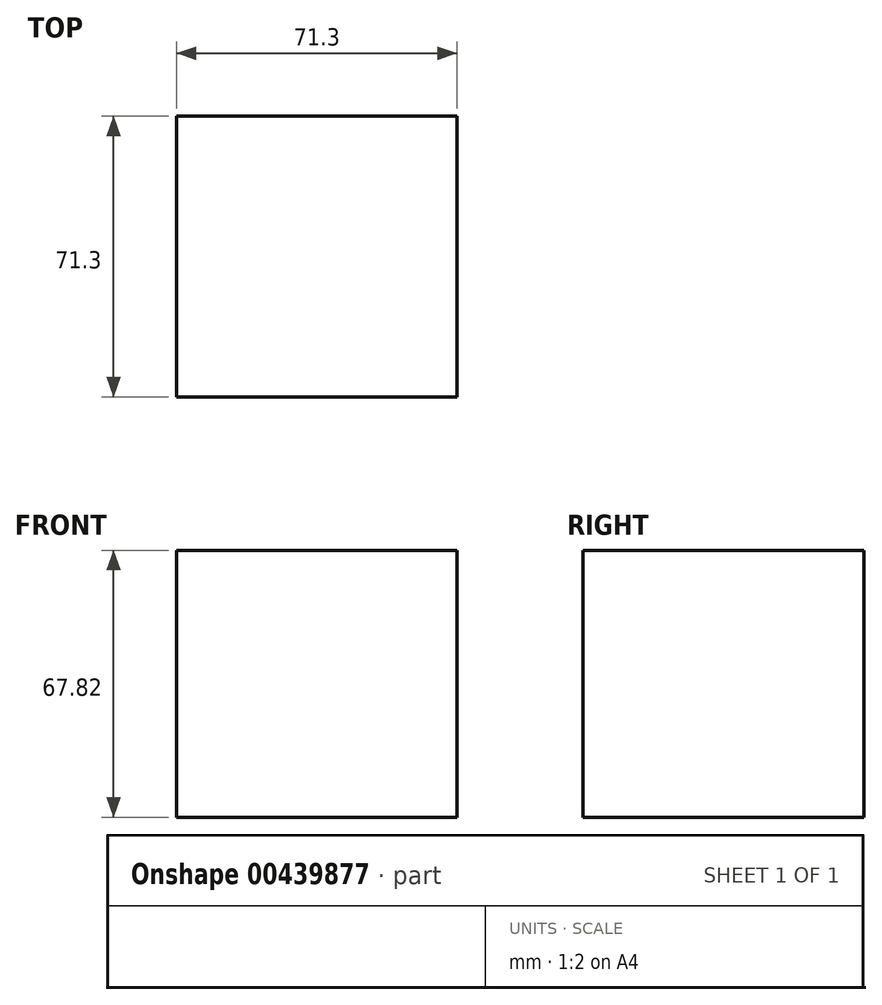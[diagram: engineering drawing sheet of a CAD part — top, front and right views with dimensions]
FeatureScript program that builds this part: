
annotation { "Feature Type Name" : "Feature", "Feature Type Description" : "" }
export const myFeature = defineFeature(function(context is Context, id is Id, definition is map)
    precondition{}
    {
        {
            var Q0;
            Q0=qCreatedBy(makeId("Top.planeOp"),FACE);
            var sketch = newSketch(context, id + "F0", { "sketchPlane" : qUnion([Q0])});
            skLineSegment(sketch, "E0.bottom", {"start": v(35.65, -35.65) * mm, "end": v(-35.65, -35.65) * mm});
            skLineSegment(sketch, "E0.top", {"start": v(35.65, 35.65) * mm, "end": v(-35.65, 35.65) * mm});
            skLineSegment(sketch, "E0.left", {"start": v(35.65, -35.65) * mm, "end": v(35.65, 35.65) * mm});
            skLineSegment(sketch, "E0.right", {"start": v(-35.65, -35.65) * mm, "end": v(-35.65, 35.65) * mm});
            skPoint(sketch, "E0.middle", {"position": v(0, 0) * mm});
            skSolve(sketch);
        }
        {
            var Q0;
            Q0=makeQuery(id+"F0.imprint","IMPRINT",FACE,{"disambiguationData":[TD([[makeQuery(id+"F0.imprint","IMPRINT",EDGE,{"derivedFrom":sQuery(id+"F0.wireOp",EDGE,"E0.bottom")}),-1.0]])]});
            extrude(context, id + "F1", {"entities" : qUnion([Q0]), "depth" : 67.82 * mm});
        }
    });
